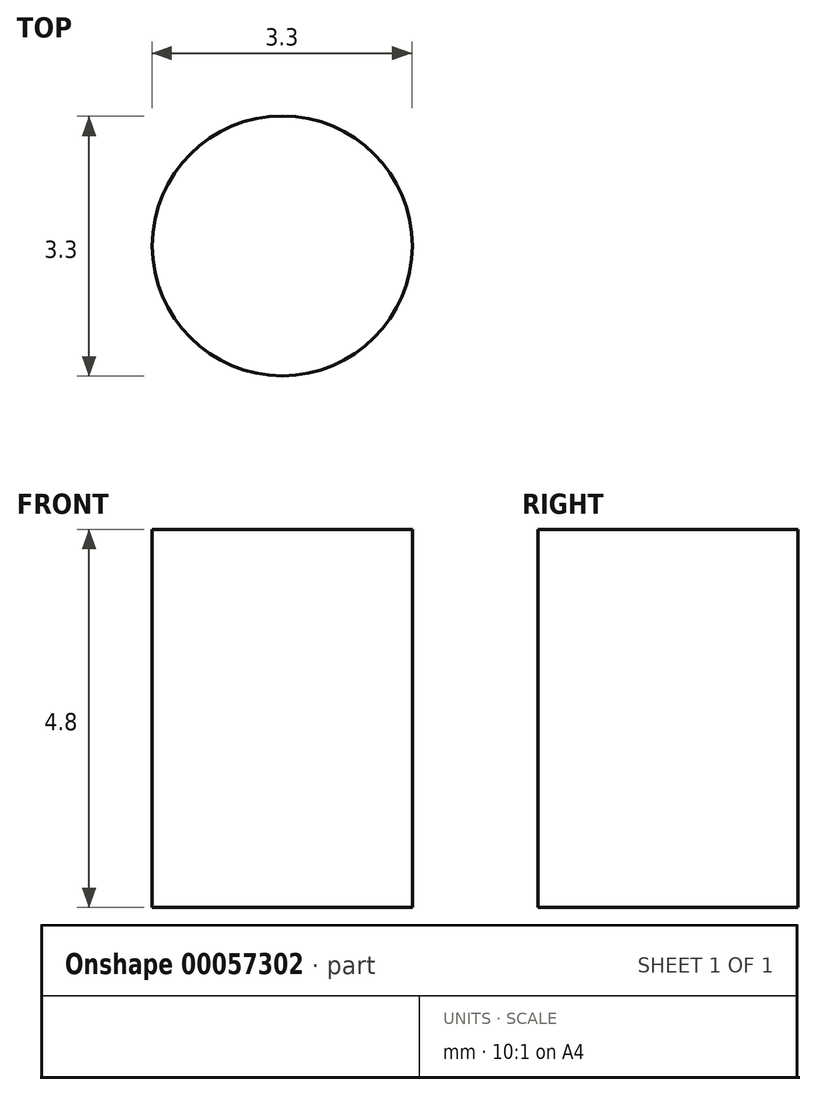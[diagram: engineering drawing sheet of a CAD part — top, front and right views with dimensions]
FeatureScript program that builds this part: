
annotation { "Feature Type Name" : "Feature", "Feature Type Description" : "" }
export const myFeature = defineFeature(function(context is Context, id is Id, definition is map)
    precondition{}
    {
        {
            var Q0;
            Q0=qCreatedBy(makeId("Top.planeOp"),FACE);
            var sketch = newSketch(context, id + "F0", { "sketchPlane" : qUnion([Q0])});
            skCircle(sketch, "E0", {"center": v(-33.15, 28.82) * mm, "radius": 1.65 * mm});
            skSolve(sketch);
        }
        {
            var Q0;
            Q0 = qSketchRegion(id + "F0", true);
            extrude(context, id + "F1", {"entities" : qUnion([Q0]), "depth" : 4.8 * mm});
        }
    });
